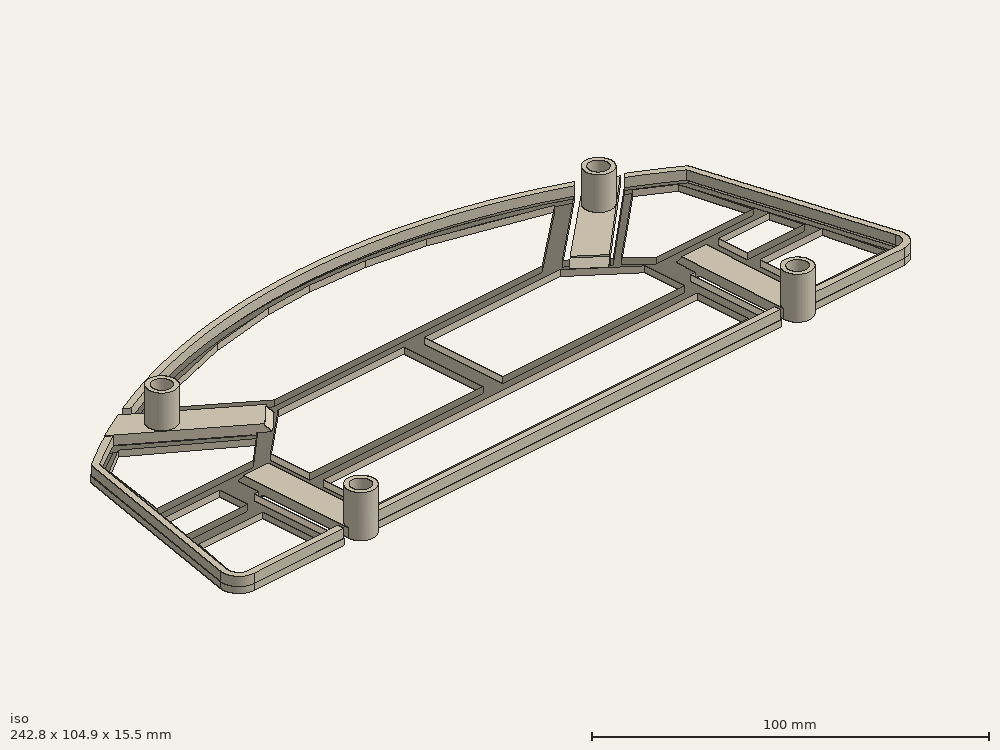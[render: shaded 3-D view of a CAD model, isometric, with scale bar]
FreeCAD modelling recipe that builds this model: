
FCSTD DOCUMENT  (FreeCAD 0.16R6045 (Git))
Label: project_n_rev4
License: All rights reserved
LicenseURL: http://en.wikipedia.org/wiki/All_rights_reserved
objects: Part::Cylinder×8, Sketcher::SketchObject×5, Part::Cut×5, Part::MultiFuse×4, Part::Chamfer×4, PartDesign::Pad×2, Part::Extrusion×2, Part::Thickness×1
note: 33 computed .brp shape members not serialized (recipe doc carries the construction recipe); baked Part::Feature solids carry a one-line shape summary decoded from their .brp

FEATURE [Sketcher::SketchObject] Sketch  label="Base"
  Placement = pos=(0,0,0) rot=(1,0,0;3.14159rad)
  sketch-geometry (71):
    g0: LineSegment StartX=-43.3507 StartY=-6.8712 StartZ=0 EndX=-28.7131 EndY=-67.7959 EndZ=0
    g1: LineSegment StartX=199.163 StartY=-6.8694 StartZ=0 EndX=184.746 EndY=-68.0609 EndZ=0
    g2: ArcOfCircle CenterX=-37.936 CenterY=-5.56776 CenterZ=0 NormalX=0 NormalY=0 NormalZ=1 Radius=5.56941 StartAngle=1.57075 EndAngle=3.37782
    g3: ArcOfCircle CenterX=193.736 CenterY=-5.5753 CenterZ=0 NormalX=0 NormalY=0 NormalZ=1 Radius=5.57903 StartAngle=6.0491 EndAngle=7.85398
    g4: ArcOfCircle CenterX=78.2135 CenterY=90.7587 CenterZ=0 NormalX=0 NormalY=0 NormalZ=1 Radius=191.24 StartAngle=4.11906 EndAngle=4.197
    g5: LineSegment StartX=-6 StartY=-32 StartZ=0 EndX=-6 EndY=0.000261594 EndZ=0
    g6: LineSegment StartX=6 StartY=-32 StartZ=0 EndX=6 EndY=0.000143702 EndZ=0
    g7: LineSegment StartX=-6 StartY=0.000261594 StartZ=0 EndX=-37.9357 EndY=0.00165396 EndZ=0
    g8: LineSegment StartX=150 StartY=-32.3968 StartZ=0 EndX=150 EndY=0.00359255 EndZ=0
    g9: LineSegment StartX=162 StartY=-32.3968 StartZ=0 EndX=161.882 EndY=0.00373137 EndZ=0
    g10: LineSegment StartX=150 StartY=0.00359255 StartZ=0 EndX=6 EndY=0.000143702 EndZ=0
    g11: LineSegment StartX=161.882 StartY=0.00373137 StartZ=0 EndX=193.736 EndY=0.00373137 EndZ=0
    g12: LineSegment StartX=-16.0434 StartY=-75.64 StartZ=0 EndX=15.3131 EndY=-52.4765 EndZ=0
    g13: LineSegment StartX=24.5337 StartY=-61.2587 StartZ=0 EndX=-3.03647 EndY=-82.3636 EndZ=0
    g14: ArcOfCircle CenterX=78.2135 CenterY=90.7587 CenterZ=0 NormalX=0 NormalY=0 NormalZ=1 Radius=191.24 StartAngle=4.27358 EndAngle=5.14801
    g15: LineSegment StartX=142 StartY=-52 StartZ=0 EndX=170.76 EndY=-76.5975 EndZ=0
    g16: LineSegment StartX=132.274 StartY=-60.4558 StartZ=0 EndX=158.911 EndY=-82.6217 EndZ=0
    g17: ArcOfCircle CenterX=78.2135 CenterY=90.7587 CenterZ=0 NormalX=0 NormalY=0 NormalZ=1 Radius=191.24 StartAngle=5.21752 EndAngle=5.30323
    g18: LineSegment StartX=5 StartY=-81.3932 StartZ=0 EndX=40.6717 EndY=-92 EndZ=0
    g19: LineSegment StartX=40.6717 StartY=-92 StartZ=0 EndX=62.6408 EndY=-95.7307 EndZ=0
    g20: LineSegment StartX=115.422 StartY=-92.1981 StartZ=0 EndX=150.549 EndY=-81.3932 EndZ=0
    g21: LineSegment StartX=150.549 StartY=-81.3932 StartZ=0 EndX=126.643 EndY=-62 EndZ=0
    g22: LineSegment StartX=126.643 StartY=-62 StartZ=0 EndX=31 EndY=-62 EndZ=0
    g23: LineSegment StartX=31 StartY=-62 StartZ=0 EndX=5 EndY=-81.3932 EndZ=0
    g24: LineSegment StartX=-10.9002 StartY=-29.4912 StartZ=0 EndX=-10.9002 EndY=-39.436 EndZ=0
    g25: LineSegment StartX=-10.9002 StartY=-39.436 StartZ=0 EndX=-30.4522 EndY=-39.436 EndZ=0
    g26: LineSegment StartX=-30.4522 StartY=-39.436 StartZ=0 EndX=-33 EndY=-29.4912 EndZ=0
    g27: LineSegment StartX=-33 StartY=-29.4912 StartZ=0 EndX=-10.9002 EndY=-29.4912 EndZ=0
    g28: LineSegment StartX=-10.9743 StartY=-5 StartZ=0 EndX=-10.9743 EndY=-24 EndZ=0
    g29: LineSegment StartX=-10.9743 StartY=-24 StartZ=0 EndX=-34 EndY=-24 EndZ=0
    g30: LineSegment StartX=-34 StartY=-24 StartZ=0 EndX=-39.0271 EndY=-5 EndZ=0
    g31: LineSegment StartX=-39.0271 StartY=-5 StartZ=0 EndX=-10.9743 EndY=-5 EndZ=0
    g32: LineSegment StartX=11.261 StartY=-6.50449 StartZ=0 EndX=11.261 EndY=-24.5558 EndZ=0
    g33: LineSegment StartX=11.261 StartY=-24.5558 StartZ=0 EndX=144.695 EndY=-24.5558 EndZ=0
    g34: LineSegment StartX=144.695 StartY=-24.5558 StartZ=0 EndX=144.695 EndY=-6.50449 EndZ=0
    g35: LineSegment StartX=144.695 StartY=-6.50449 StartZ=0 EndX=11.261 EndY=-6.50449 EndZ=0
    g36: LineSegment StartX=167.644 StartY=-25.2876 StartZ=0 EndX=190 EndY=-25.2876 EndZ=0
    g37: LineSegment StartX=190 StartY=-25.2876 StartZ=0 EndX=193.482 EndY=-6.26056 EndZ=0
    g38: LineSegment StartX=193.482 StartY=-6.26056 StartZ=0 EndX=167.644 EndY=-6.26056 EndZ=0
    g39: LineSegment StartX=167.644 StartY=-6.26056 StartZ=0 EndX=167.644 EndY=-25.2876 EndZ=0
    g40: LineSegment StartX=167.848 StartY=-40.4117 StartZ=0 EndX=186 EndY=-40.4117 EndZ=0
    g41: LineSegment StartX=186 StartY=-40.4117 StartZ=0 EndX=188.115 EndY=-29.9242 EndZ=0
    g42: LineSegment StartX=188.115 StartY=-29.9242 StartZ=0 EndX=167.848 EndY=-29.9242 EndZ=0
    g43: LineSegment StartX=167.848 StartY=-29.9242 StartZ=0 EndX=167.848 EndY=-40.4117 EndZ=0
    g44: LineSegment StartX=-28.746 StartY=-44 StartZ=0 EndX=-24 EndY=-65.8046 EndZ=0
    g45: LineSegment StartX=-24 StartY=-65.8046 StartZ=0 EndX=-14.6261 EndY=-71.8385 EndZ=0
    g46: LineSegment StartX=-14.6261 StartY=-71.8385 StartZ=0 EndX=14 EndY=-51.3805 EndZ=0
    g47: LineSegment StartX=14 StartY=-51.3805 StartZ=0 EndX=5.55797 EndY=-44 EndZ=0
    g48: LineSegment StartX=5.55797 StartY=-44 StartZ=0 EndX=-28.746 EndY=-44 EndZ=0
    g49: LineSegment StartX=184.574 StartY=-44.6904 StartZ=0 EndX=150 EndY=-44.6904 EndZ=0
    g50: LineSegment StartX=150 StartY=-44.6904 StartZ=0 EndX=143.578 EndY=-50.7188 EndZ=0
    g51: LineSegment StartX=143.578 StartY=-50.7188 StartZ=0 EndX=170 EndY=-73 EndZ=0
    g52: LineSegment StartX=170 StartY=-73 StartZ=0 EndX=180 EndY=-66.7707 EndZ=0
    g53: LineSegment StartX=180 StartY=-66.7707 StartZ=0 EndX=184.574 EndY=-44.6904 EndZ=0
    g54: LineSegment StartX=73 StartY=-29.4733 StartZ=0 EndX=73 EndY=-57.6014 EndZ=0
    g55: LineSegment StartX=73 StartY=-57.6014 StartZ=0 EndX=28 EndY=-57.6014 EndZ=0
    g56: LineSegment StartX=28 StartY=-57.6014 StartZ=0 EndX=11.2554 EndY=-43.539 EndZ=0
    g57: LineSegment StartX=11.2554 StartY=-43.539 StartZ=0 EndX=11.2554 EndY=-29.4733 EndZ=0
    g58: LineSegment StartX=11.2554 StartY=-29.4733 StartZ=0 EndX=73 EndY=-29.4733 EndZ=0
    g59: LineSegment StartX=80.0378 StartY=-29.4766 StartZ=0 EndX=80.0378 EndY=-57.4378 EndZ=0
    g60: LineSegment StartX=80.0378 StartY=-57.4378 StartZ=0 EndX=128.477 EndY=-57.4378 EndZ=0
    g61: LineSegment StartX=128.477 StartY=-57.4378 StartZ=0 EndX=145 EndY=-43.7025 EndZ=0
    g62: LineSegment StartX=145 StartY=-43.7025 StartZ=0 EndX=145 EndY=-29.4766 EndZ=0
    g63: LineSegment StartX=145 StartY=-29.4766 StartZ=0 EndX=80.0378 EndY=-29.4766 EndZ=0
    g64: LineSegment StartX=62.6408 StartY=-95.7307 StartZ=0 EndX=78 EndY=-96.5296 EndZ=0
    g65: LineSegment StartX=78 StartY=-96.5296 StartZ=0 EndX=97 EndY=-95.3313 EndZ=0
    g66: LineSegment StartX=97 StartY=-95.3313 StartZ=0 EndX=115.422 EndY=-92.1981 EndZ=0
    g67: LineSegment StartX=-6 StartY=-32 StartZ=0 EndX=6 EndY=-32 EndZ=0
    g68: LineSegment StartX=150 StartY=-32.3968 StartZ=0 EndX=162 EndY=-32.3968 EndZ=0
    g69: LineSegment StartX=15.3131 StartY=-52.4765 StartZ=0 EndX=24.5337 EndY=-61.2587 EndZ=0
    g70: LineSegment StartX=132.274 StartY=-60.4558 StartZ=0 EndX=142 EndY=-52 EndZ=0
  constraints (100):
    c: Coincident(g4,g0)
    c: Coincident(g17,g1)
    c: PointOnObject(g13,g4)
    c: Coincident(g4,g12)
    c: PointOnObject(g15,g14)
    c: Coincident(g14,g16)
    c: Coincident(g6,g10)
    c: Coincident(g9,g11)
    c: Coincident(g5,g7)
    c: Coincident(g10,g8)
    c: Coincident(g13,g14)
    c: Coincident(g15,g17)
    c: Coincident(g0,g2)
    c: Coincident(g3,g1)
    c: Coincident(g2,g7)
    c: Coincident(g3,g11)
    c: Coincident(g18,g19)
    c: Coincident(g66,g20)
    c: Coincident(g20,g21)
    c: Coincident(g21,g22)
    c: Horizontal(g22)
    c: Coincident(g22,g23)
    c: Coincident(g23,g18)
    c: Vertical(g24)
    c: Coincident(g24,g25)
    c: Horizontal(g25)
    c: Coincident(g25,g26)
    c: Coincident(g26,g27)
    c: Coincident(g27,g24)
    c: Horizontal(g27)
    c: Vertical(g28)
    c: Coincident(g28,g29)
    c: Horizontal(g29)
    c: Coincident(g29,g30)
    c: Coincident(g31,g30)
    c: Coincident(g31,g28)
    c: Horizontal(g31)
    c: Vertical(g32)
    c: Coincident(g32,g33)
    c: Horizontal(g33)
    c: Coincident(g33,g34)
    c: Vertical(g34)
    c: Coincident(g34,g35)
    c: Coincident(g35,g32)
    c: Horizontal(g35)
    c: Horizontal(g36)
    c: Coincident(g36,g37)
    c: Coincident(g37,g38)
    c: Horizontal(g38)
    c: Coincident(g38,g39)
    c: Coincident(g39,g36)
    c: Vertical(g39)
    c: Horizontal(g40)
    c: Coincident(g40,g41)
    c: Coincident(g41,g42)
    c: Horizontal(g42)
    c: Coincident(g42,g43)
    c: Coincident(g43,g40)
    c: Vertical(g43)
    c: Coincident(g44,g45)
    c: Coincident(g45,g46)
    c: Coincident(g46,g47)
    c: Coincident(g48,g47)
    c: Coincident(g48,g44)
    c: Horizontal(g48)
    c: Horizontal(g49)
    c: Coincident(g49,g50)
    c: Coincident(g50,g51)
    c: Coincident(g51,g52)
    c: Coincident(g52,g53)
    c: Coincident(g53,g49)
    c: Vertical(g54)
    c: Coincident(g54,g55)
    c: Horizontal(g55)
    c: Coincident(g55,g56)
    c: Coincident(g56,g57)
    c: Vertical(g57)
    c: Coincident(g57,g58)
    c: Coincident(g58,g54)
    c: Horizontal(g58)
    c: Vertical(g59)
    c: Coincident(g59,g60)
    c: Horizontal(g60)
    c: Coincident(g60,g61)
    c: Coincident(g61,g62)
    c: Vertical(g62)
    c: Coincident(g62,g63)
    c: Coincident(g63,g59)
    c: Horizontal(g63)
    c: Coincident(g64,g65)
    c: Coincident(g19,g64)
    c: Coincident(g66,g65)
    c: Coincident(g67,g5)
    c: Coincident(g67,g6)
    c: Horizontal(g67)
    c: Coincident(g68,g8)
    c: Coincident(g68,g9)
    c: Horizontal(g68)
    c: Coincident(g70,g16)
    c: Coincident(g70,g15)
FEATURE [Sketcher::SketchObject] Sketch004  label="Wall"
  sketch-geometry (29):
    g0: ArcOfCircle CenterX=78.2135 CenterY=90.7587 CenterZ=0 NormalX=0 NormalY=0 NormalZ=1 Radius=191.194 StartAngle=4.13378 EndAngle=4.19443
    g1: LineSegment StartX=-6 StartY=0 StartZ=0 EndX=-38 EndY=0 EndZ=0
    g2: LineSegment StartX=150 StartY=0 StartZ=0 EndX=5.75606 EndY=0 EndZ=0
    g3: LineSegment StartX=162 StartY=0 StartZ=0 EndX=193.736 EndY=0 EndZ=0
    g4: ArcOfCircle CenterX=78.3526 CenterY=90.8251 CenterZ=0 NormalX=0 NormalY=0 NormalZ=1 Radius=191.182 StartAngle=4.31861 EndAngle=5.10486
    g5: ArcOfCircle CenterX=78.2135 CenterY=90.7587 CenterZ=0 NormalX=0 NormalY=0 NormalZ=1 Radius=190.959 StartAngle=5.22699 EndAngle=5.28539
    g6: LineSegment StartX=5 StartY=-83 StartZ=0 EndX=39.505 EndY=-94 EndZ=0
    g7: LineSegment StartX=39.505 StartY=-94 StartZ=0 EndX=62.585 EndY=-98 EndZ=0
    g8: LineSegment StartX=115.781 StartY=-94.1981 StartZ=0 EndX=151.474 EndY=-83.5973 EndZ=0
    g9: LineSegment StartX=-38 StartY=-3.39482 StartZ=0 EndX=-6 EndY=-3.39482 EndZ=0
    g10: LineSegment StartX=149.756 StartY=-3.59354 StartZ=0 EndX=5.75606 EndY=-3.59354 EndZ=0
    g11: LineSegment StartX=193.736 StartY=-4.18044 StartZ=0 EndX=162 EndY=-4.18044 EndZ=0
    g12: LineSegment StartX=-24.7851 StartY=-67 StartZ=0 EndX=-14.3428 EndY=-73.6141 EndZ=0
    g13: LineSegment StartX=171 StartY=-74 StartZ=0 EndX=181 EndY=-67.7707 EndZ=0
    g14: LineSegment StartX=62.585 StartY=-98 StartZ=0 EndX=78 EndY=-98.5838 EndZ=0
    g15: LineSegment StartX=78 StartY=-98.5838 StartZ=0 EndX=97.359 EndY=-97.3313 EndZ=0
    g16: LineSegment StartX=97.359 StartY=-97.3313 StartZ=0 EndX=115.781 EndY=-94.1981 EndZ=0
    g17: LineSegment StartX=-6 StartY=0 StartZ=0 EndX=-6 EndY=-3.39482 EndZ=0
    g18: LineSegment StartX=5.75606 StartY=-3.59354 StartZ=0 EndX=5.75606 EndY=0 EndZ=0
    g19: LineSegment StartX=-38 StartY=0 StartZ=0 EndX=-38 EndY=-3.39482 EndZ=0
    g20: LineSegment StartX=150 StartY=0 StartZ=0 EndX=149.756 EndY=-3.59354 EndZ=0
    g21: LineSegment StartX=162 StartY=0 StartZ=0 EndX=162 EndY=-4.18044 EndZ=0
    g22: LineSegment StartX=193.736 StartY=0 StartZ=0 EndX=193.736 EndY=-4.18044 EndZ=0
    g23: LineSegment StartX=5 StartY=-83 StartZ=0 EndX=5 EndY=-85.7248 EndZ=0
    g24: LineSegment StartX=151.474 StartY=-83.5973 StartZ=0 EndX=151.474 EndY=-85.8208 EndZ=0
    g25: LineSegment StartX=171 StartY=-74 StartZ=0 EndX=172.201 EndY=-75.469 EndZ=0
    g26: LineSegment StartX=181 StartY=-67.7707 StartZ=0 EndX=181.744 EndY=-69.6997 EndZ=0
    g27: LineSegment StartX=-14.3428 StartY=-73.6141 StartZ=0 EndX=-16.4482 EndY=-75.3566 EndZ=0
    g28: LineSegment StartX=-24.7851 StartY=-67 StartZ=0 EndX=-26.3433 EndY=-69.3132 EndZ=0
  constraints (39):
    c: Coincident(g6,g7)
    c: Coincident(g16,g8)
    c: Horizontal(g9)
    c: Horizontal(g10)
    c: Horizontal(g11)
    c: Coincident(g14,g15)
    c: Coincident(g7,g14)
    c: Coincident(g16,g15)
    c: Coincident(g17,g1)
    c: Coincident(g17,g9)
    c: Vertical(g17)
    c: Coincident(g18,g10)
    c: Coincident(g18,g2)
    c: Vertical(g18)
    c: Coincident(g19,g1)
    c: Coincident(g19,g9)
    c: Vertical(g19)
    c: Coincident(g20,g2)
    c: Coincident(g20,g10)
    c: Coincident(g21,g3)
    c: Coincident(g21,g11)
    c: Vertical(g21)
    c: Coincident(g22,g3)
    c: Coincident(g22,g11)
    c: Vertical(g22)
    c: Coincident(g23,g6)
    c: Coincident(g23,g4)
    c: Vertical(g23)
    c: Coincident(g24,g8)
    c: Coincident(g24,g4)
    c: Vertical(g24)
    c: Coincident(g25,g13)
    c: Coincident(g25,g5)
    c: Coincident(g26,g13)
    c: Coincident(g26,g5)
    c: Coincident(g27,g12)
    c: Coincident(g27,g0)
    c: Coincident(g28,g12)
    c: Coincident(g28,g0)
FEATURE [Sketcher::SketchObject] Sketch006
  Placement = pos=(0,0,0) rot=(1,0,0;3.14159rad)
  sketch-geometry (10):
    g0: LineSegment StartX=-43.3507 StartY=-6.8712 StartZ=0 EndX=-28.6056 EndY=-67.6363 EndZ=0
    g1: LineSegment StartX=199.163 StartY=-6.8694 StartZ=0 EndX=184.746 EndY=-68.0609 EndZ=0
    g2: ArcOfCircle CenterX=-37.936 CenterY=-5.56776 CenterZ=0 NormalX=0 NormalY=0 NormalZ=1 Radius=5.56941 StartAngle=1.57075 EndAngle=3.37782
    g3: ArcOfCircle CenterX=193.736 CenterY=-5.5753 CenterZ=0 NormalX=0 NormalY=0 NormalZ=1 Radius=5.57903 StartAngle=6.0491 EndAngle=7.85398
    g4: ArcOfCircle CenterX=78.6813 CenterY=91.7773 CenterZ=0 NormalX=0 NormalY=0 NormalZ=1 Radius=192.154 StartAngle=4.12001 EndAngle=4.26651
    g5: LineSegment StartX=6 StartY=-0.234337 StartZ=0 EndX=-37.9357 EndY=0.00165396 EndZ=0
    g6: LineSegment StartX=161.599 StartY=-0.204933 StartZ=0 EndX=6 EndY=-0.234337 EndZ=0
    g7: LineSegment StartX=161.599 StartY=-0.204933 StartZ=0 EndX=193.736 EndY=0.00373137 EndZ=0
    g8: ArcOfCircle CenterX=78.463 CenterY=91.7918 CenterZ=0 NormalX=0 NormalY=0 NormalZ=1 Radius=192.073 StartAngle=4.26756 EndAngle=5.14419
    g9: ArcOfCircle CenterX=78.2123 CenterY=90.7613 CenterZ=0 NormalX=0 NormalY=0 NormalZ=1 Radius=191.243 StartAngle=5.14763 EndAngle=5.30323
  constraints (10):
    c: Coincident(g4,g0)
    c: Coincident(g9,g1)
    c: Coincident(g0,g2)
    c: Coincident(g3,g1)
    c: Coincident(g2,g5)
    c: Coincident(g3,g7)
    c: Coincident(g5,g6)
    c: Coincident(g6,g7)
    c: Coincident(g8,g9)
    c: Coincident(g4,g8)
FEATURE [PartDesign::Pad] Pad
  Length = 5
  Length2 = 100
  Placement = pos=(0,0,0) rot=(1,0,0;3.14159rad)
  Reversed = true
  Sketch = -> Sketch006
  Type = 0
FEATURE [Part::Thickness] Thickness
  Faces = -> Pad [Face11,Face12]
  Intersection = false
  Join = 0
  Mode = 1
  SelfIntersection = false
  Value = -2
FEATURE [Part::Extrusion] Extrude
  Base = -> Sketch
  Dir = (0,0,2)
  Solid = true
FEATURE [Part::Cylinder] Cylinder
  Angle = 360
  Height = 14
  Placement = pos=(0,0,1.5) rot=(0,0,1;0rad)
  Radius = 4.4
FEATURE [Part::Cylinder] Cylinder004
  Angle = 360
  Height = 12
  Placement = pos=(0,0,3.5) rot=(0,0,1;0rad)
  Radius = 3
FEATURE [Part::Cylinder] Cylinder001
  Angle = 360
  Height = 14
  Placement = pos=(155.8,0,1.5) rot=(0,0,1;0rad)
  Radius = 4.4
FEATURE [Part::Cylinder] Cylinder005
  Angle = 360
  Height = 12
  Placement = pos=(155.8,0,3.5) rot=(0,0,1;0rad)
  Radius = 3
FEATURE [Part::Cylinder] Cylinder002
  Angle = 360
  Height = 14
  Placement = pos=(155.8,71,1.5) rot=(0,0,1;0rad)
  Radius = 4.4
FEATURE [Part::Cylinder] Cylinder006
  Angle = 360
  Height = 12
  Placement = pos=(155.8,71,3.5) rot=(0,0,1;0rad)
  Radius = 3
FEATURE [Part::Cylinder] Cylinder003
  Angle = 360
  Height = 14
  Placement = pos=(0,71,1.5) rot=(0,0,1;0rad)
  Radius = 4.4
FEATURE [Part::Cylinder] Cylinder007
  Angle = 360
  Height = 12
  Placement = pos=(0,71,3.5) rot=(0,0,1;0rad)
  Radius = 3
FEATURE [Sketcher::SketchObject] Sketch007  label="Springy thing"
  Placement = pos=(0,0,1.5) rot=(1,0,0;3.14159rad)
  sketch-geometry (16):
    g0: LineSegment StartX=-4.40208 StartY=0 StartZ=0 EndX=-4.40208 EndY=-37.5004 EndZ=0
    g1: LineSegment StartX=4.40547 StartY=0 StartZ=0 EndX=4.40547 EndY=-37.5004 EndZ=0
    g2: LineSegment StartX=151.442 StartY=0 StartZ=0 EndX=151.761 EndY=-37.3467 EndZ=0
    g3: LineSegment StartX=160.216 StartY=0 StartZ=0 EndX=160.535 EndY=-37.3467 EndZ=0
    g4: LineSegment StartX=-15 StartY=-76.3521 StartZ=0 EndX=17.8292 EndY=-52.1593 EndZ=0
    g5: LineSegment StartX=-5.23652 StartY=-81.4351 StartZ=0 EndX=24.952 EndY=-58.8018 EndZ=0
    g6: ArcOfCircle CenterX=78.1816 CenterY=90.7137 CenterZ=0 NormalX=0 NormalY=0 NormalZ=1 Radius=191.295 StartAngle=4.20361 EndAngle=4.26116
    g7: LineSegment StartX=169.644 StartY=-77.1363 StartZ=0 EndX=139.631 EndY=-51 EndZ=0
    g8: LineSegment StartX=161 StartY=-81.5613 StartZ=0 EndX=132 EndY=-57.3864 EndZ=0
    g9: ArcOfCircle CenterX=78.2183 CenterY=90.7977 CenterZ=0 NormalX=0 NormalY=0 NormalZ=1 Radius=191.208 StartAngle=5.16014 EndAngle=5.21093
    g10: LineSegment StartX=151.442 StartY=0 StartZ=0 EndX=160.216 EndY=0 EndZ=0
    g11: LineSegment StartX=-4.40208 StartY=0 StartZ=0 EndX=4.40547 EndY=0 EndZ=0
    g12: LineSegment StartX=-4.40208 StartY=-37.5004 StartZ=0 EndX=4.40547 EndY=-37.5004 EndZ=0
    g13: LineSegment StartX=17.8292 StartY=-52.1593 StartZ=0 EndX=24.952 EndY=-58.8018 EndZ=0
    g14: LineSegment StartX=139.631 StartY=-51 StartZ=0 EndX=132 EndY=-57.3864 EndZ=0
    g15: LineSegment StartX=151.761 StartY=-37.3467 StartZ=0 EndX=160.535 EndY=-37.3467 EndZ=0
  constraints (19):
    c: Coincident(g6,g4)
    c: Coincident(g9,g8)
    c: Coincident(g5,g6)
    c: Coincident(g7,g9)
    c: Coincident(g10,g2)
    c: Coincident(g10,g3)
    c: Coincident(g11,g0)
    c: Coincident(g11,g1)
    c: Horizontal(g11)
    c: Coincident(g12,g0)
    c: Coincident(g12,g1)
    c: Horizontal(g12)
    c: Coincident(g13,g4)
    c: Coincident(g13,g5)
    c: Coincident(g14,g7)
    c: Coincident(g14,g8)
    c: Coincident(g15,g2)
    c: Coincident(g15,g3)
    c: Horizontal(g15)
FEATURE [Part::Extrusion] Extrude001
  Base = -> Sketch007
  Dir = (0,0,3)
  Solid = true
FEATURE [Part::MultiFuse] Fusion
  Shapes = -> [Extrude,Extrude001]
FEATURE [Part::Chamfer] Chamfer
  Base = -> Fusion
  Edges = 1 edges r=2: [Edge97]
FEATURE [Part::Chamfer] Chamfer001
  Base = -> Chamfer
  Edges = 1 edges r=2: [Edge16]
FEATURE [Part::Chamfer] Chamfer002
  Base = -> Chamfer001
  Edges = 2 edges r=2: [Edge27,Edge42]
FEATURE [Part::Chamfer] Chamfer003
  Base = -> Chamfer002
  Edges = 4 edges r=1.4: [Edge106,Edge124,Edge150,Edge179]
FEATURE [Sketcher::SketchObject] Sketch011
  Placement = pos=(0,0,0) rot=(1,0,0;3.14159rad)
  sketch-geometry (17):
    g0: LineSegment StartX=-17 StartY=-77 StartZ=0 EndX=-16.2168 EndY=-75.7568 EndZ=0
    g1: LineSegment StartX=-16.2168 StartY=-75.7568 StartZ=0 EndX=-13.3538 EndY=-73.5849 EndZ=0
    g2: LineSegment StartX=-13.3538 StartY=-73.5849 StartZ=0 EndX=-0.371851 EndY=-80.4461 EndZ=0
    g3: LineSegment StartX=-0.371851 StartY=-80.4461 StartZ=0 EndX=-4.37011 EndY=-83.7039 EndZ=0
    g4: LineSegment StartX=-4.37011 StartY=-83.7039 StartZ=0 EndX=-17 EndY=-77 EndZ=0
    g5: LineSegment StartX=171.197 StartY=-77 StartZ=0 EndX=168.944 EndY=-75 EndZ=0
    g6: LineSegment StartX=168.944 StartY=-75 StartZ=0 EndX=157 EndY=-81 EndZ=0
    g7: LineSegment StartX=157 StartY=-81 StartZ=0 EndX=161 EndY=-84.5874 EndZ=0
    g8: LineSegment StartX=161 StartY=-84.5874 StartZ=0 EndX=171.197 EndY=-77 EndZ=0
    g9: LineSegment StartX=150 StartY=0.629851 StartZ=0 EndX=150 EndY=-3.46712 EndZ=0
    g10: LineSegment StartX=150 StartY=-3.46712 StartZ=0 EndX=162 EndY=-3.46712 EndZ=0
    g11: LineSegment StartX=162 StartY=-3.46712 StartZ=0 EndX=162 EndY=2.35749 EndZ=0
    g12: LineSegment StartX=162 StartY=2.35749 StartZ=0 EndX=150 EndY=0.629851 EndZ=0
    g13: LineSegment StartX=-6 StartY=1.22898 StartZ=0 EndX=-6 EndY=-5 EndZ=0
    g14: LineSegment StartX=-6 StartY=-5 StartZ=0 EndX=6 EndY=-5 EndZ=0
    g15: LineSegment StartX=6 StartY=-5 StartZ=0 EndX=6 EndY=2.75918 EndZ=0
    g16: LineSegment StartX=6 StartY=2.75918 StartZ=0 EndX=-6 EndY=1.22898 EndZ=0
  constraints (23):
    c: Coincident(g0,g1)
    c: Coincident(g1,g2)
    c: Coincident(g2,g3)
    c: Coincident(g3,g4)
    c: Coincident(g4,g0)
    c: Coincident(g5,g6)
    c: Coincident(g6,g7)
    c: Coincident(g7,g8)
    c: Coincident(g8,g5)
    c: Vertical(g9)
    c: Coincident(g9,g10)
    c: Horizontal(g10)
    c: Coincident(g10,g11)
    c: Vertical(g11)
    c: Coincident(g11,g12)
    c: Coincident(g12,g9)
    c: Vertical(g13)
    c: Coincident(g13,g14)
    c: Horizontal(g14)
    c: Coincident(g14,g15)
    c: Vertical(g15)
    c: Coincident(g15,g16)
    c: Coincident(g16,g13)
FEATURE [PartDesign::Pad] Pad001
  Length = 10
  Length2 = 100
  Placement = pos=(0,0,0) rot=(1,0,0;3.14159rad)
  Reversed = true
  Sketch = -> Sketch011
  Type = 0
FEATURE [Part::Cut] Cut
  Base = -> Thickness
  Tool = -> Pad001
FEATURE [Part::Cut] Cut001
  Base = -> Cylinder
  Tool = -> Cylinder004
FEATURE [Part::Cut] Cut002
  Base = -> Cylinder002
  Tool = -> Cylinder006
FEATURE [Part::Cut] Cut003
  Base = -> Cylinder003
  Tool = -> Cylinder007
FEATURE [Part::Cut] Cut004
  Base = -> Cylinder001
  Tool = -> Cylinder005
FEATURE [Part::MultiFuse] Fusion001  label="Legs"
  Shapes = -> [Cut001,Cut003,Cut004,Cut002]
FEATURE [Part::MultiFuse] Fusion002
  Shapes = -> [Cut,Chamfer003]
FEATURE [Part::MultiFuse] Fusion003
  Shapes = -> [Fusion001,Fusion002]
